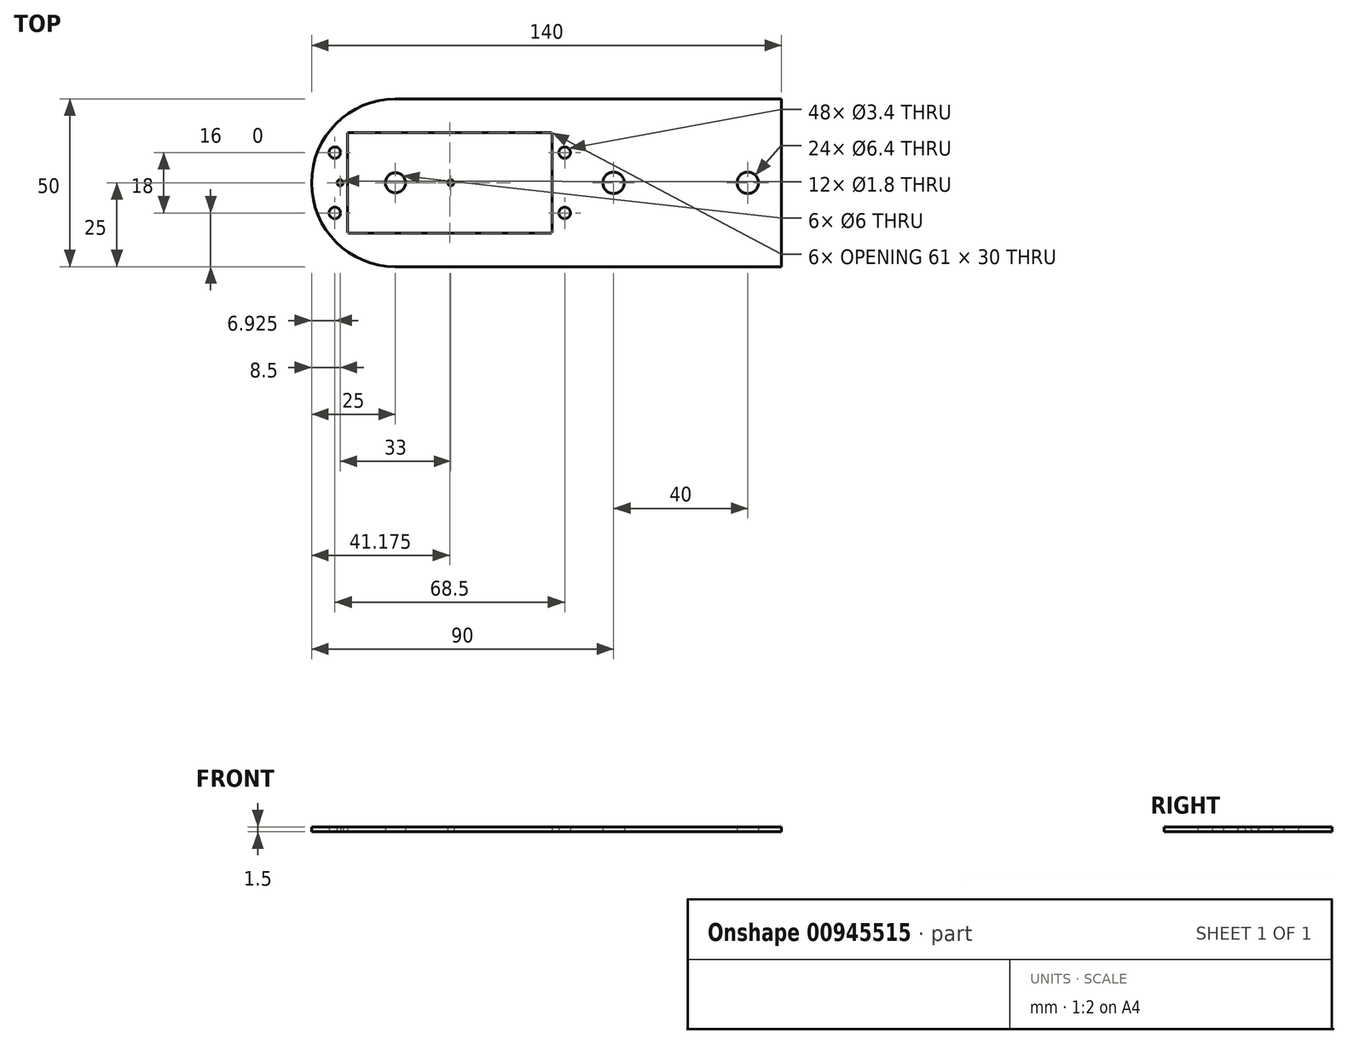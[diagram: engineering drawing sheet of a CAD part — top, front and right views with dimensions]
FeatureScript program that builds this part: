
annotation { "Feature Type Name" : "Feature", "Feature Type Description" : "" }
export const myFeature = defineFeature(function(context is Context, id is Id, definition is map)
    precondition{}
    {
        {
            var Q0;
            Q0=qCreatedBy(makeId("Top.planeOp"),FACE);
            var sketch = newSketch(context, id + "F0", { "sketchPlane" : qUnion([Q0])});
            skLineSegment(sketch, "E0.bottom", {"start": v(70, 25) * mm, "end": v(-45, 25) * mm});
            skLineSegment(sketch, "E0.top", {"start": v(70, -25) * mm, "end": v(-45, -25) * mm});
            skLineSegment(sketch, "E0.left", {"start": v(70, 25) * mm, "end": v(70, -25) * mm});
            skLineSegment(sketch, "E0.right", {"start": v(-70, 0) * mm, "end": v(-70, 0) * mm});
            skPoint(sketch, "E0.middle", {"position": v(0, 0) * mm});
            skCircle(sketch, "E1", {"center": v(20, 0) * mm, "radius": 3.2 * mm});
            skCircle(sketch, "E2", {"center": v(60, 0) * mm, "radius": 3.2 * mm});
            skPoint(sketch, "E3.visualSharp", {"position": v(-70, 25) * mm});
            skArc(sketch, "E3.filletArc", {"start": v(-45, 25) * mm, "mid": v(-62.68, 17.68) * mm, "end": v(-70, 0) * mm});
            skPoint(sketch, "E4.visualSharp", {"position": v(-70, -25) * mm});
            skArc(sketch, "E4.filletArc", {"start": v(-70, 0) * mm, "mid": v(-62.68, -17.68) * mm, "end": v(-45, -25) * mm});
            skCircle(sketch, "E5", {"center": v(-45, 0) * mm, "radius": 3 * mm});
            skCircle(sketch, "E6", {"center": v(-63.07, 9) * mm, "radius": 1.7 * mm});
            skCircle(sketch, "E7", {"center": v(-63.07, -9) * mm, "radius": 1.7 * mm});
            skCircle(sketch, "E8", {"center": v(5.43, 9) * mm, "radius": 1.7 * mm});
            skCircle(sketch, "E9", {"center": v(5.43, -9) * mm, "radius": 1.7 * mm});
            skCircle(sketch, "E10", {"center": v(-28.5, 0) * mm, "radius": 0.9 * mm});
            skCircle(sketch, "E11", {"center": v(-61.5, 0) * mm, "radius": 0.9 * mm});
            skSolve(sketch);
        }
        {
            var Q0;
            Q0=makeQuery(id+"F0.imprint","IMPRINT",FACE,{"disambiguationData":[TD([[makeQuery(id+"F0.imprint","IMPRINT",EDGE,{"derivedFrom":sQuery(id+"F0.wireOp",EDGE,"E0.bottom")}),1.0]])]});
            extrude(context, id + "F1", {"entities" : qUnion([Q0]), "depth" : 1.5 * mm, "offsetDistance" : 25 * mm});
        }
        {
            var Q0;
            Q0=qCreatedBy(makeId("Top.planeOp"),FACE);
            var sketch = newSketch(context, id + "F2", { "sketchPlane" : qUnion([Q0])});
            skLineSegment(sketch, "E12.bottom", {"start": v(70, 25) * mm, "end": v(-45, 25) * mm});
            skLineSegment(sketch, "E12.top", {"start": v(70, -25) * mm, "end": v(-45, -25) * mm});
            skLineSegment(sketch, "E12.left", {"start": v(70, 25) * mm, "end": v(70, -25) * mm});
            skLineSegment(sketch, "E12.right", {"start": v(-70, 0) * mm, "end": v(-70, 0) * mm});
            skPoint(sketch, "E12.middle", {"position": v(0, 0) * mm});
            skCircle(sketch, "E13.MirrorC", {"center": v(5.42, 9) * mm, "radius": 1.7 * mm});
            skCircle(sketch, "E14.MirrorC", {"center": v(5.42, -9) * mm, "radius": 1.7 * mm});
            skCircle(sketch, "E15.MirrorC", {"center": v(-45, 0.17) * mm, "radius": 8.81 * mm});
            skCircle(sketch, "E16.MirrorC", {"center": v(-63.08, -9) * mm, "radius": 1.7 * mm});
            skCircle(sketch, "E17.MirrorC", {"center": v(-63.08, 9) * mm, "radius": 1.7 * mm});
            skPoint(sketch, "E18.visualSharp", {"position": v(-70, 25) * mm});
            skArc(sketch, "E18.filletArc", {"start": v(-45, 25) * mm, "mid": v(-62.68, 17.68) * mm, "end": v(-70, 0) * mm});
            skPoint(sketch, "E19.visualSharp", {"position": v(-70, -25) * mm});
            skArc(sketch, "E19.filletArc", {"start": v(-70, 0) * mm, "mid": v(-62.68, -17.68) * mm, "end": v(-45, -25) * mm});
            skCircle(sketch, "E20", {"center": v(20, 0) * mm, "radius": 3.2 * mm});
            skCircle(sketch, "E21", {"center": v(60, 0) * mm, "radius": 3.2 * mm});
            skLineSegment(sketch, "E22.bottom", {"start": v(1.67, 15) * mm, "end": v(-59.33, 15) * mm});
            skLineSegment(sketch, "E22.top", {"start": v(1.67, -15) * mm, "end": v(-59.32, -15) * mm});
            skLineSegment(sketch, "E22.left", {"start": v(1.67, 15) * mm, "end": v(1.67, -15) * mm});
            skLineSegment(sketch, "E22.right", {"start": v(-59.33, 15) * mm, "end": v(-59.32, -15) * mm});
            skLineSegment(sketch, "E23", {"start": v(-28.83, 15) * mm, "end": v(-28.82, -15) * mm});
            skSolve(sketch);
        }
        {
            var Q0;
            Q0 = qSketchRegion(id + "F2", true);
            extrude(context, id + "F3", {"entities" : qUnion([Q0]), "depth" : 1.5 * mm, "offsetDistance" : 25 * mm});
        }
        {
            var Q0;
            Q0=makeQuery(id+"F3.opExtrude","SWEPT_EDGE",EDGE,{"disambiguationData":[OSD([sQuery(id+"F2.wireOp",EDGE,"E22.bottom"),sQuery(id+"F2.wireOp",EDGE,"E22.right")])]});
            var Q1;
            Q1=makeQuery(id+"F3.opExtrude","SWEPT_EDGE",EDGE,{"disambiguationData":[OSD([sQuery(id+"F2.wireOp",EDGE,"E22.top"),sQuery(id+"F2.wireOp",EDGE,"E22.right")])]});
            var Q2;
            Q2=makeQuery(id+"F3.opExtrude","SWEPT_EDGE",EDGE,{"disambiguationData":[OSD([sQuery(id+"F2.wireOp",EDGE,"E22.top"),sQuery(id+"F2.wireOp",EDGE,"E22.left")])]});
            var Q3;
            Q3=makeQuery(id+"F3.opExtrude","SWEPT_EDGE",EDGE,{"disambiguationData":[OSD([sQuery(id+"F2.wireOp",EDGE,"E22.bottom"),sQuery(id+"F2.wireOp",EDGE,"E22.left")])]});
            fillet(context, id + "F4", {"entities" : qUnion([Q0, Q1, Q2, Q3]), "radius" : 0.5 * mm, "tangentPropagation" : true, "allowEdgeOverflow" : false});
        }
    });
